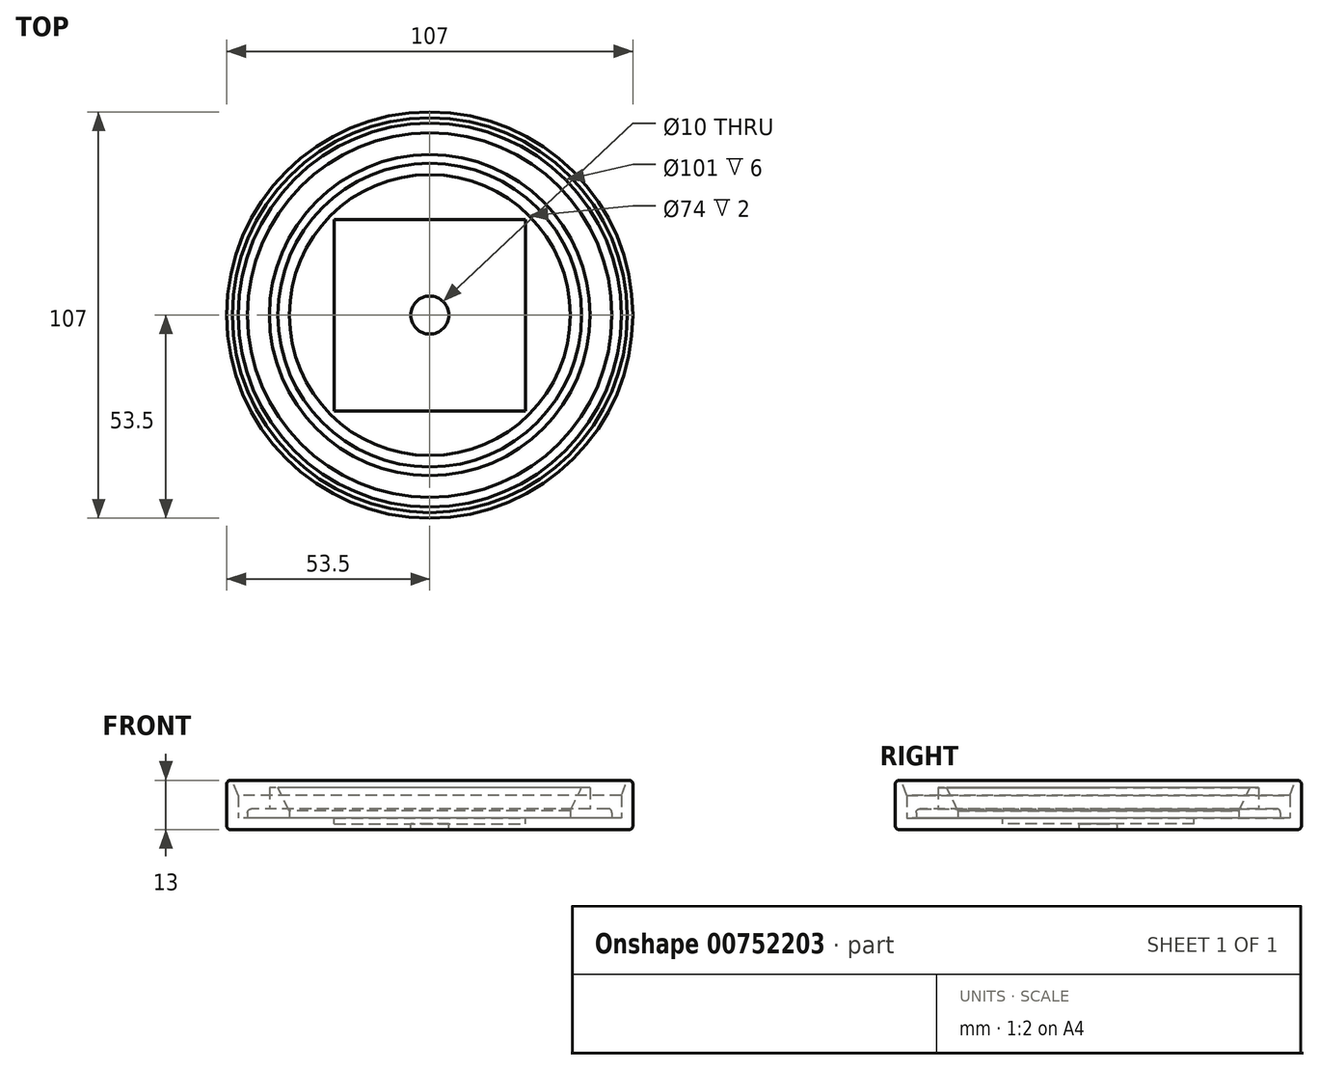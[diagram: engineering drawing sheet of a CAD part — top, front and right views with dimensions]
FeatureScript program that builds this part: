
annotation { "Feature Type Name" : "Feature", "Feature Type Description" : "" }
export const myFeature = defineFeature(function(context is Context, id is Id, definition is map)
    precondition{}
    {
        {
            var Q0;
            Q0=qCreatedBy(makeId("Top.planeOp"),FACE);
            var sketch = newSketch(context, id + "F0", { "sketchPlane" : qUnion([Q0])});
            skCircle(sketch, "E0", {"center": v(0, 0) * mm, "radius": 53.5 * mm});
            skSolve(sketch);
        }
        {
            var Q0;
            Q0=makeQuery(id+"F0.imprint","IMPRINT",FACE,{"disambiguationData":[TD([[makeQuery(id+"F0.imprint","IMPRINT",EDGE,{"derivedFrom":sQuery(id+"F0.wireOp",EDGE,"E0")}),1.0]])]});
            extrude(context, id + "F1", {"entities" : qUnion([Q0]), "depth" : 13 * mm, "offsetDistance" : 25 * mm});
        }
        {
            var Q0;
            Q0=makeQuery(id+"F1.opExtrude","CAP_FACE",FACE,{"disambiguationData":[OSD([sQuery(id+"F0.wireOp",EDGE,"E0")])],"isStart":false});
            shell(context, id + "F2", {"entities" : qUnion([Q0]), "thickness" : 3 * mm});
        }
        {
            var Q0;
            {var subQ0=sQuery(id+"F0.wireOp",EDGE,"E0");Q0=makeQuery(id+"F2.opShell","OFFSET_FACE",FACE,{"disambiguationData":[OSD([subQ0]),TDD([makeQuery(id+"F1.opExtrude","CAP_FACE",FACE,{"disambiguationData":[OSD([subQ0])],"isStart":true})])]});}
            var sketch = newSketch(context, id + "F3", { "sketchPlane" : qUnion([Q0])});
            skCircle(sketch, "E1", {"center": v(0, 0) * mm, "radius": 48 * mm});
            skCircle(sketch, "E2", {"center": v(0, 0) * mm, "radius": 42.25 * mm});
            skCircle(sketch, "E3", {"center": v(0, 0) * mm, "radius": 37 * mm});
            skSolve(sketch);
        }
        {
            var Q0;
            Q0=makeQuery(id+"F3.imprint","IMPRINT",FACE,{"disambiguationData":[TD([[makeQuery(id+"F3.imprint","IMPRINT",EDGE,{"derivedFrom":sQuery(id+"F3.wireOp",EDGE,"E1")}),1.0]])]});
            var Q1;
            Q1=makeQuery(id+"F3.imprint","IMPRINT",FACE,{"disambiguationData":[TD([[makeQuery(id+"F3.imprint","IMPRINT",EDGE,{"derivedFrom":sQuery(id+"F3.wireOp",EDGE,"E2")}),1.0]])]});
            extrude(context, id + "F4", {"entities" : qUnion([Q0, Q1]), "operationType" : NewBodyOperationType.ADD, "depth" : 2.5 * mm, "offsetDistance" : 25 * mm});
        }
        {
            var Q0;
            Q0=makeQuery(id+"F3.imprint","IMPRINT",FACE,{"disambiguationData":[TD([[makeQuery(id+"F3.imprint","IMPRINT",EDGE,{"derivedFrom":sQuery(id+"F3.wireOp",EDGE,"E2")}),1.0]])]});
            extrude(context, id + "F5", {"entities" : qUnion([Q0]), "operationType" : NewBodyOperationType.ADD, "depth" : 8 * mm, "offsetDistance" : 25 * mm});
        }
        {
            var Q0;
            Q0=makeQuery(id+"F5.opExtrude","CAP_EDGE",EDGE,{"disambiguationData":[OSD([sQuery(id+"F3.wireOp",EDGE,"E3")])],"isStart":false});
            chamfer(context, id + "F6", {"entities" : qUnion([Q0]), "chamferType" : ChamferType.TWO_OFFSETS, "width1" : 3 * mm, "oppositeDirection" : true, "width2" : 6 * mm, "tangentPropagation" : true});
        }
        {
            var Q0;
            {var subQ0=sQuery(id+"F0.wireOp",EDGE,"E0");Q0=makeQuery(id+"F2.opShell","OFFSET_EDGE",EDGE,{"disambiguationData":[OSD([subQ0]),TDD([makeQuery(id+"F1.opExtrude","CAP_EDGE",EDGE,{"disambiguationData":[OSD([subQ0])],"isStart":false})])]});}
            chamfer(context, id + "F7", {"entities" : qUnion([Q0]), "chamferType" : ChamferType.TWO_OFFSETS, "width1" : 4 * mm, "oppositeDirection" : false, "width2" : 1.5 * mm, "tangentPropagation" : true});
        }
        {
            var Q0;
            Q0=makeQuery(id+"F4.opExtrude","CAP_EDGE",EDGE,{"disambiguationData":[OSD([sQuery(id+"F3.wireOp",EDGE,"E1")])],"isStart":false});
            var Q1;
            Q1=makeQuery(id+"F1.opExtrude","CAP_EDGE",EDGE,{"disambiguationData":[OSD([sQuery(id+"F0.wireOp",EDGE,"E0")])],"isStart":true});
            var Q2;
            Q2=makeQuery(id+"F1.opExtrude","CAP_EDGE",EDGE,{"disambiguationData":[OSD([sQuery(id+"F0.wireOp",EDGE,"E0")])],"isStart":false});
            fillet(context, id + "F8", {"entities" : qUnion([Q0, Q1, Q2]), "radius" : 1 * mm, "tangentPropagation" : true, "allowEdgeOverflow" : false});
        }
        {
            var Q0;
            Q0=makeQuery(id+"F4.opExtrude","CAP_FACE",FACE,{"disambiguationData":[OSD([sQuery(id+"F3.wireOp",EDGE,"E1")])],"isStart":false});
            var sketch = newSketch(context, id + "F9", { "sketchPlane" : qUnion([Q0])});
            skCircle(sketch, "E4", {"center": v(0, 0) * mm, "radius": 5 * mm});
            skSolve(sketch);
        }
        {
            var Q0;
            Q0 = qSketchRegion(id + "F9", true);
            extrude(context, id + "F10", {"entities" : qUnion([Q0]), "operationType" : NewBodyOperationType.REMOVE, "endBound" : BoundingType.SYMMETRIC, "oppositeDirection" : true, "depth" : 91.4 * mm, "offsetDistance" : 25 * mm});
        }
        {
            var Q0;
            Q0=makeQuery(id+"F3.imprint","IMPRINT",FACE,{"disambiguationData":[TD([[makeQuery(id+"F3.imprint","IMPRINT",EDGE,{"derivedFrom":sQuery(id+"F3.wireOp",EDGE,"E3")}),1.0]])]});
            var sketch = newSketch(context, id + "F11", { "sketchPlane" : qUnion([Q0])});
            skLineSegment(sketch, "E5.bottom", {"start": v(-25.2, 25.2) * mm, "end": v(25.2, 25.2) * mm});
            skLineSegment(sketch, "E5.top", {"start": v(-25.2, -25.2) * mm, "end": v(25.2, -25.2) * mm});
            skLineSegment(sketch, "E5.left", {"start": v(-25.2, 25.2) * mm, "end": v(-25.2, -25.2) * mm});
            skLineSegment(sketch, "E5.right", {"start": v(25.2, 25.2) * mm, "end": v(25.2, -25.2) * mm});
            skPoint(sketch, "E5.middle", {"position": v(0, 0) * mm});
            skSolve(sketch);
        }
        {
            var Q0;
            {var subQ1=makeQuery(id+"F3.imprint","IMPRINT",EDGE,{"derivedFrom":sQuery(id+"F3.wireOp",EDGE,"E3")});var subQ10=sQuery(id+"F11.wireOp",EDGE,"E5.bottom");var subQ11=makeQuery(id+"F11.imprint","INTERSECT",VERTEX,{"disambiguationData":[OD(0.0)],"derivedFrom":[subQ1,subQ10]});Q0=makeQuery(id+"F11.imprint","IMPRINT",FACE,{"disambiguationData":[TD([[makeQuery(id+"F11.imprint","IMPRINT",EDGE,{"disambiguationData":[TD([[subQ11,-1.0]])],"derivedFrom":subQ10}),-1.0]])]});}
            extrude(context, id + "F12", {"entities" : qUnion([Q0]), "operationType" : NewBodyOperationType.REMOVE, "oppositeDirection" : true, "depth" : 1.5 * mm, "offsetDistance" : 25 * mm});
        }
    });
